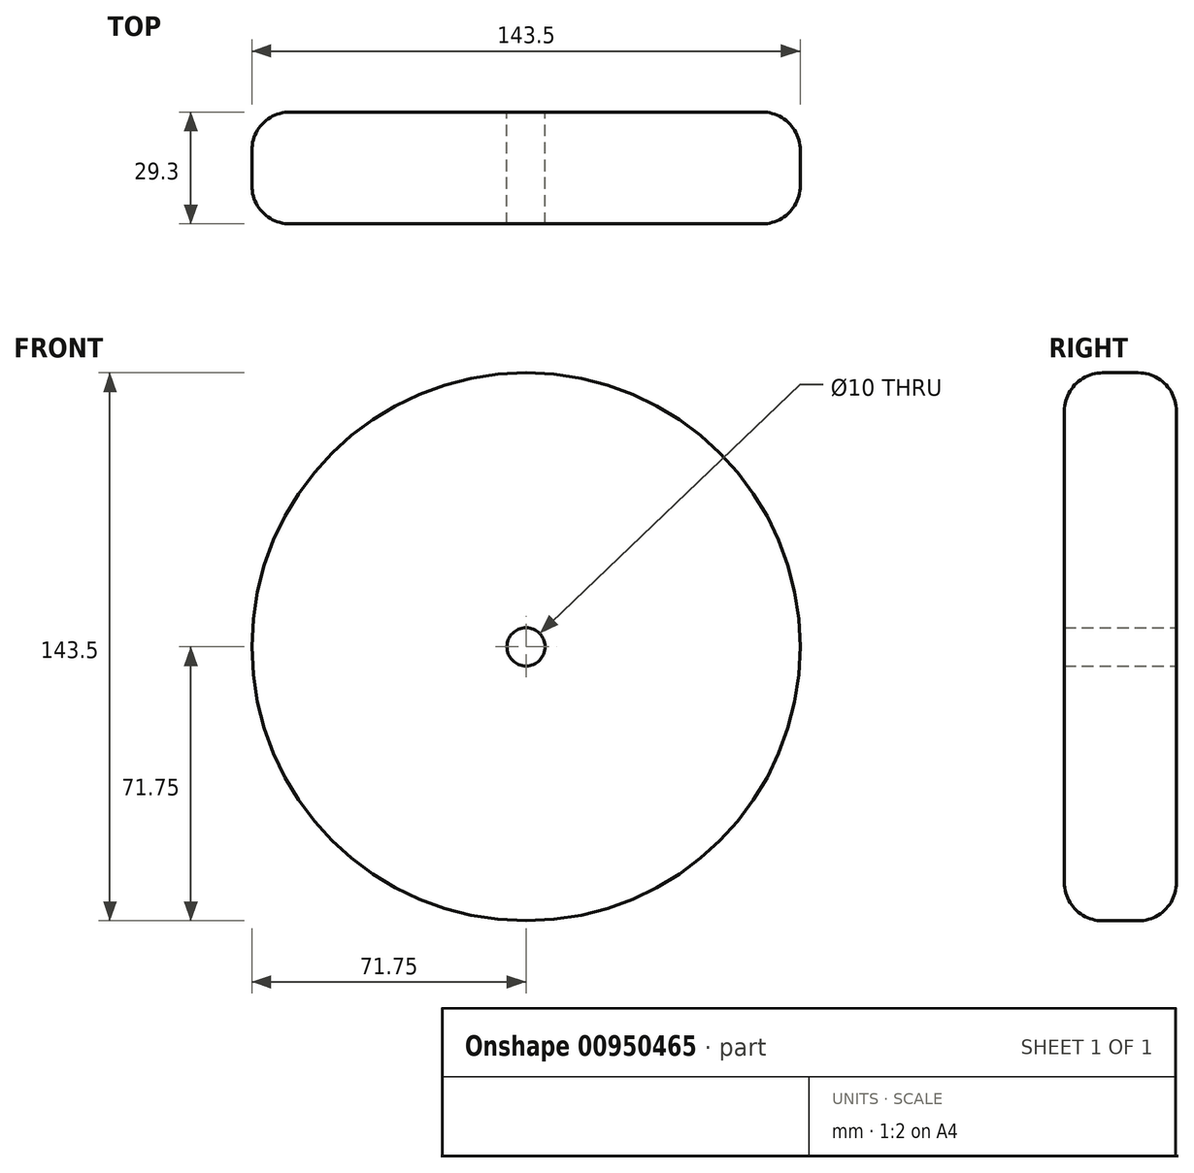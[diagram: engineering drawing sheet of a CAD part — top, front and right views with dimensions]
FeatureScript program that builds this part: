
annotation { "Feature Type Name" : "Feature", "Feature Type Description" : "" }
export const myFeature = defineFeature(function(context is Context, id is Id, definition is map)
    precondition{}
    {
        {
            var Q0;
            Q0=qCreatedBy(makeId("Front.planeOp"),FACE);
            var sketch = newSketch(context, id + "F0", { "sketchPlane" : qUnion([Q0])});
            skCircle(sketch, "E0", {"center": v(0, 0) * mm, "radius": 71.75 * mm});
            skCircle(sketch, "E1", {"center": v(0, 0) * mm, "radius": 5 * mm});
            skSolve(sketch);
        }
        {
            var Q0;
            Q0=qSketchRegion(id+"F0",true);
            extrude(context, id + "F1", {"entities" : qUnion([Q0]), "depth" : 29.3 * mm, "offsetDistance" : 25 * mm});
        }
        {
            var Q0;
            Q0=makeQuery(id+"F1.opExtrude","CAP_EDGE",EDGE,{"disambiguationData":[OSD([sQuery(id+"F0.wireOp",EDGE,"E0")])],"isStart":false});
            var Q1;
            Q1=makeQuery(id+"F1.opExtrude","CAP_EDGE",EDGE,{"disambiguationData":[OSD([sQuery(id+"F0.wireOp",EDGE,"E0")])],"isStart":true});
            fillet(context, id + "F2", {"entities" : qUnion([Q0, Q1]), "radius" : 10 * mm, "tangentPropagation" : true, "allowEdgeOverflow" : false});
        }
    });
